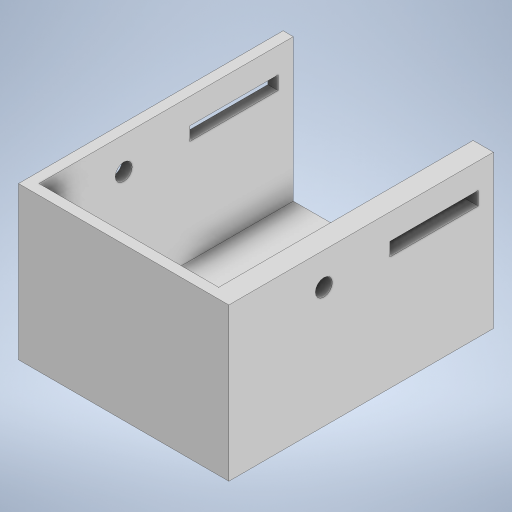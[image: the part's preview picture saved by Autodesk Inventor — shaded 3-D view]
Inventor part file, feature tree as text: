
AUTODESK INVENTOR PART (.ipt)
format: ipt  version: 2023 (Build 270158000, 158)  size: 231,424 bytes
history: native  units: in
note: dims shown in document units (in); Inventor stores cm internally (conversion verified against a paired STEP export)
features: sketch x6, extrude x5, shell x1
ambient origin geometry x8: Origin, YZ Plane, XZ Plane, XY Plane, X Axis, Y Axis, Z Axis, Center Point
bodies: Solid1 (feature_tree)
feature tree (12):
  extrude  "Extrusion1"  Depth=3.0709in
  shell  "Shell1"  Thickness=1.7717in
  sketch  "Sketch4"  dims[d4=0.1181in d17=0.3937in d18=0.0in]
  extrude  "Extrusion3"  Depth=0.3937in TaperAngle=0.0deg
  sketch  "Sketch6"  dims[d21=0.1772in d22=1.3189in]
  extrude  "Extrusion5"  Depth=0.1575in
  extrude  "Extrusion6"  Depth=1.3189in
  extrude  "Extrusion7"  TaperAngle=0.0deg  [1 undecoded]
  sketch  "Sketch2"  dims[d0=2.3228in d1=3.0709in d2=1.7717in d3=0.0in]
  sketch  "Sketch5"  dims[d19=1.0236in d20=0.1575in]
  sketch  "Sketch7"  dims[d25=0.1181in d26=0.0in d27=0.0in d28=0.0in]
  sketch  "Sketch8"  dims[d29=0.1969in d30=0.0in d31=0.0in d13=0.0197in d14=0.0344in d15=0.0197in d16=0.0344in]
note: 1 required parameter value undecoded (feature->parameter linkage not recoverable at this tier; creation-order binding heuristic only, values carry confidence <= 0.55)
